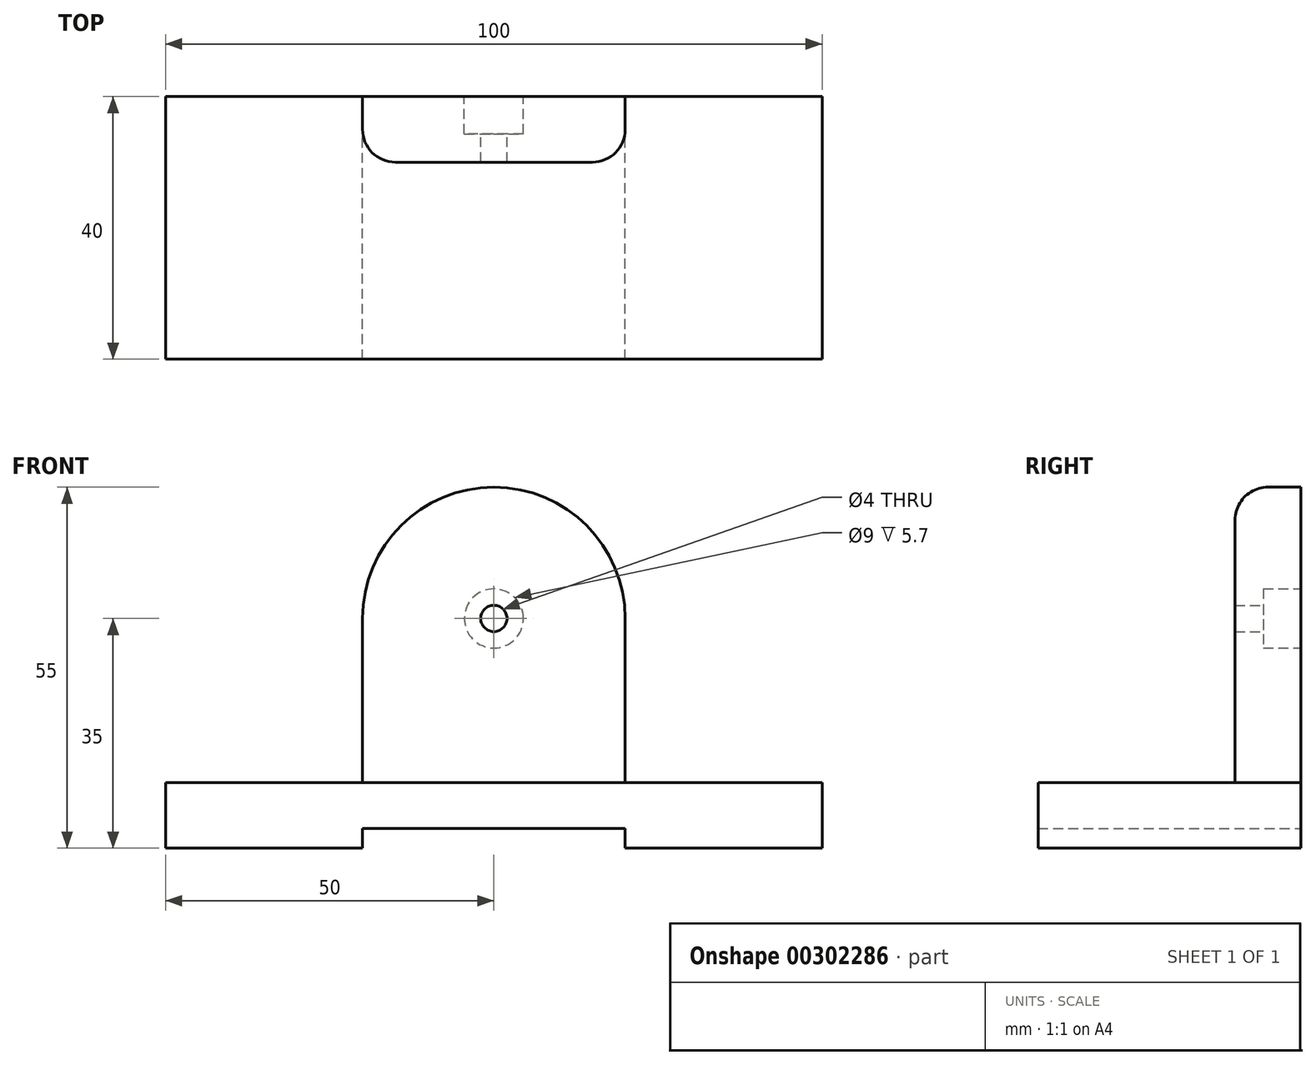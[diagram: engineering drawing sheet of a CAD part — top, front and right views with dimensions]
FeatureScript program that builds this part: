
annotation { "Feature Type Name" : "Feature", "Feature Type Description" : "" }
export const myFeature = defineFeature(function(context is Context, id is Id, definition is map)
    precondition{}
    {
        {
            var Q0;
            Q0=qCreatedBy(makeId("Top.planeOp"),FACE);
            var sketch = newSketch(context, id + "F0", { "sketchPlane" : qUnion([Q0])});
            skLineSegment(sketch, "E0.bottom", {"start": v(0, 0) * mm, "end": v(-100, 0) * mm});
            skLineSegment(sketch, "E0.top", {"start": v(0, 40) * mm, "end": v(-100, 40) * mm});
            skLineSegment(sketch, "E0.left", {"start": v(0, 0) * mm, "end": v(0, 40) * mm});
            skLineSegment(sketch, "E0.right", {"start": v(-100, 0) * mm, "end": v(-100, 40) * mm});
            skSolve(sketch);
        }
        {
            var Q0;
            Q0 = qSketchRegion(id + "F0", true);
            extrude(context, id + "F1", {"entities" : qUnion([Q0]), "depth" : 10 * mm});
        }
        {
            var Q0;
            Q0=makeQuery(id+"F1.opExtrude","SWEPT_FACE",FACE,{"disambiguationData":[OSD([sQuery(id+"F0.wireOp",EDGE,"E0.top")])]});
            var sketch = newSketch(context, id + "F2", { "sketchPlane" : qUnion([Q0])});
            skLineSegment(sketch, "E1", {"start": v(30, 0) * mm, "end": v(30, 35) * mm});
            skArc(sketch, "E2", {"start": v(30, 35) * mm, "mid": v(50, 55) * mm, "end": v(70, 35) * mm});
            skLineSegment(sketch, "E3", {"start": v(70, 35) * mm, "end": v(70, 0) * mm});
            skLineSegment(sketch, "E4", {"start": v(30, 0) * mm, "end": v(70, 0) * mm});
            skSolve(sketch);
        }
        {
            var Q0;
            Q0 = qSketchRegion(id + "F2", true);
            extrude(context, id + "F3", {"entities" : qUnion([Q0]), "operationType" : NewBodyOperationType.ADD, "oppositeDirection" : true, "depth" : 10 * mm});
        }
        {
            var Q0;
            Q0=makeQuery(id+"F3.boolean.opBoolean","MERGE",FACE,{"derivedFrom":[makeQuery(id+"F1.opExtrude","SWEPT_FACE",FACE,{"disambiguationData":[OSD([sQuery(id+"F0.wireOp",EDGE,"E0.top")])]}),makeQuery(id+"F3.opExtrude","CAP_FACE",FACE,{"disambiguationData":[OSD([sQuery(id+"F2.wireOp",EDGE,"E1"),sQuery(id+"F2.wireOp",EDGE,"E2"),sQuery(id+"F2.wireOp",EDGE,"E3"),sQuery(id+"F2.wireOp",EDGE,"E4")])],"isStart":true})]});
            var sketch = newSketch(context, id + "F4", { "sketchPlane" : qUnion([Q0])});
            skCircle(sketch, "E5", {"center": v(50, 35) * mm, "radius": 2 * mm});
            skSolve(sketch);
        }
        {
            var Q0;
            Q0 = qSketchRegion(id + "F4", true);
            extrude(context, id + "F5", {"entities" : qUnion([Q0]), "operationType" : NewBodyOperationType.REMOVE, "oppositeDirection" : true, "depth" : 25 * mm});
        }
        {
            var Q0;
            Q0=makeQuery(id+"F3.boolean.opBoolean","MERGE",FACE,{"derivedFrom":[makeQuery(id+"F1.opExtrude","SWEPT_FACE",FACE,{"disambiguationData":[OSD([sQuery(id+"F0.wireOp",EDGE,"E0.top")])]}),makeQuery(id+"F3.opExtrude","CAP_FACE",FACE,{"disambiguationData":[OSD([sQuery(id+"F2.wireOp",EDGE,"E1"),sQuery(id+"F2.wireOp",EDGE,"E2"),sQuery(id+"F2.wireOp",EDGE,"E3"),sQuery(id+"F2.wireOp",EDGE,"E4")])],"isStart":true})]});
            var sketch = newSketch(context, id + "F6", { "sketchPlane" : qUnion([Q0])});
            skCircle(sketch, "E6", {"center": v(50, 35) * mm, "radius": 4.5 * mm});
            skSolve(sketch);
        }
        {
            var Q0;
            Q0 = qSketchRegion(id + "F6", true);
            extrude(context, id + "F7", {"entities" : qUnion([Q0]), "operationType" : NewBodyOperationType.REMOVE, "oppositeDirection" : true, "depth" : 5.7 * mm});
        }
        {
            var Q0;
            Q0=makeQuery(id+"F3.boolean.opBoolean","MERGE",FACE,{"derivedFrom":[makeQuery(id+"F1.opExtrude","SWEPT_FACE",FACE,{"disambiguationData":[OSD([sQuery(id+"F0.wireOp",EDGE,"E0.top")])]}),makeQuery(id+"F3.opExtrude","CAP_FACE",FACE,{"disambiguationData":[OSD([sQuery(id+"F2.wireOp",EDGE,"E1"),sQuery(id+"F2.wireOp",EDGE,"E2"),sQuery(id+"F2.wireOp",EDGE,"E3"),sQuery(id+"F2.wireOp",EDGE,"E4")])],"isStart":true})]});
            var sketch = newSketch(context, id + "F8", { "sketchPlane" : qUnion([Q0])});
            skLineSegment(sketch, "E7.bottom", {"start": v(30, 3) * mm, "end": v(70, 3) * mm});
            skLineSegment(sketch, "E7.top", {"start": v(30, 0) * mm, "end": v(70, 0) * mm});
            skLineSegment(sketch, "E7.left", {"start": v(30, 3) * mm, "end": v(30, 0) * mm});
            skLineSegment(sketch, "E7.right", {"start": v(70, 3) * mm, "end": v(70, 0) * mm});
            skSolve(sketch);
        }
        {
            var Q0;
            Q0 = qSketchRegion(id + "F8", true);
            extrude(context, id + "F9", {"entities" : qUnion([Q0]), "operationType" : NewBodyOperationType.REMOVE, "endBound" : BoundingType.THROUGH_ALL, "oppositeDirection" : true, "depth" : 25 * mm});
        }
        {
            var Q0;
            Q0=makeQuery(id+"F3.opExtrude","CAP_EDGE",EDGE,{"disambiguationData":[OSD([sQuery(id+"F2.wireOp",EDGE,"E3")])],"isStart":false});
            var Q1;
            Q1=makeQuery(id+"F3.opExtrude","CAP_EDGE",EDGE,{"disambiguationData":[OSD([sQuery(id+"F2.wireOp",EDGE,"E1")])],"isStart":false});
            fillet(context, id + "F10", {"entities" : qUnion([Q0, Q1]), "radius" : 5 * mm, "tangentPropagation" : true, "allowEdgeOverflow" : false});
        }
    });
